# Revit family: TD92_FOR811_CIN210_RVT20_R00
name_source: partatom
category: Mobiliário
units: mm (PartAtom-declared; Revit-internal decimal feet)

## family parameters
Com base no plano de trabalho = Não
Compartilhado = Não
Corte com vazios quando carregada = Não
Número OmniClass = 23.40.20.00
Ponto de cálculo do ambiente = Não
Sempre na vertical = Sim
Título OmniClass = General Furniture and Specialties

## types (1)
- TD92_FOR811_CIN210_RVT20_R00
    Descrição = Pensando em aliar um produto funcional com um visual de bom gosto, a Tramontina lança a linha T-Force de lixeiras. Com a Lixeira Tramontina T-Force 15L em Polipropileno, você vai ter uma peça funcional que traz praticidade aos ambientes. É uma lixeira articulável com tampa acionada por pedal. Além disso, facilita na hora da limpeza devido a superfície lisa. Comporta 15 litros.
    Elevação padrão = 0  [stored 0 ft]
    Fabricante = Tramontina Delta S/A
    Modelo = Lixeira Tramontina T-Force 15L em Polipropileno Cinza
    Nota-chave = 92811210
    URL = Lixeira Tramontina T-Force 15L em Polipropileno Cinza

note: [stored X ft] marks values corroborated as IEEE doubles in the binary element streams (Revit-internal decimal feet)
